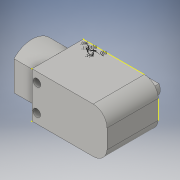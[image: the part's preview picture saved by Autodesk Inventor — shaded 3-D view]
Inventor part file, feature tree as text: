
AUTODESK INVENTOR PART (.ipt)
format: ipt  version: 2016 (Build 200138000, 138)  size: 161,280 bytes
history: native  units: in
note: dims shown in document units (in); Inventor stores cm internally (conversion verified against a paired STEP export)
features: extrude x6, sketch x5
ambient origin geometry x8: Origin, YZ Plane, XZ Plane, XY Plane, X Axis, Y Axis, Z Axis, Center Point
bodies: Solid1 (feature_tree)
feature tree (11):
  extrude  "Extrusion1"  Depth=1.0in TaperAngle=0.0deg
  sketch  "Sketch2"  dims[d10=0.37in d11=0.27in]
  sketch  "Sketch3"  dims[d12=0.27in d13=0.096in]
  sketch  "Sketch4"  dims[d14=0.188in d15=0.148in]
  extrude  "Extrusion5"  Depth=0.27in
  extrude  "Extrusion6"  Depth=0.27in
  extrude  "Extrusion7"  Depth=0.148in
  extrude  "Extrusion8"  Depth=0.3in
  extrude  "Extrusion9"  Depth=0.3in
  sketch  "Sketch1"  dims[d3=0.887in d4=1.0in d5=0.0in]
  sketch  "Sketch5"  dims[d16=0.116in d17=0.018in d18=0.089in d23=0.35in d24=0.398in d32=1.0in d33=0.0in d34=1.0in d35=0.0in d36=0.5in d37=0.0in d39=0.887in d41=0.148in d42=0.5in d43=0.0in d45=0.186in d46=0.183in d47=0.183in d48=0.277in d49=0.3in d50=0.0in]
